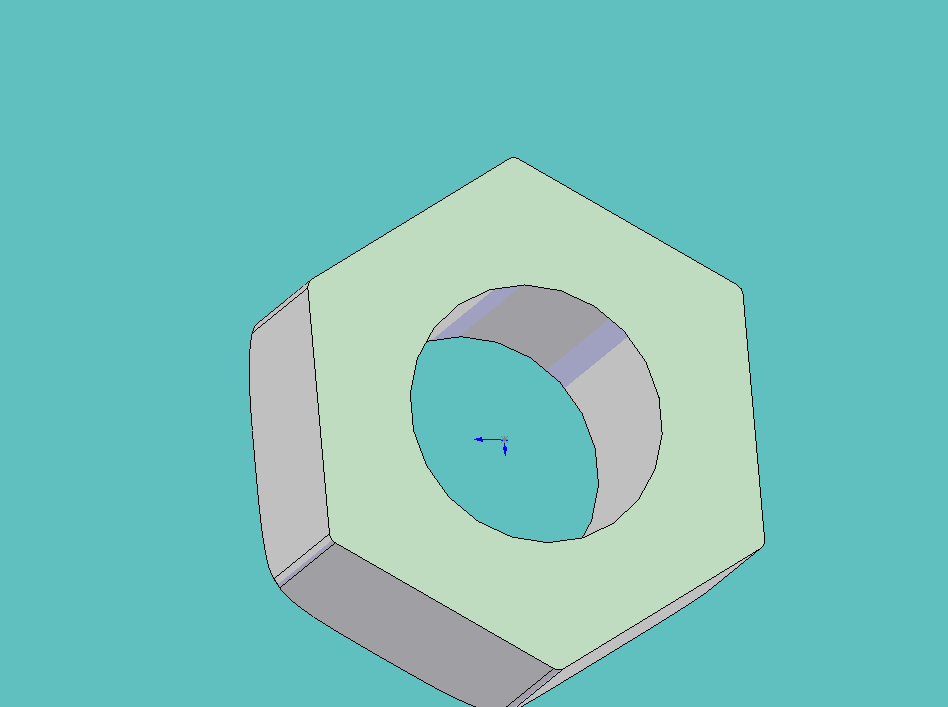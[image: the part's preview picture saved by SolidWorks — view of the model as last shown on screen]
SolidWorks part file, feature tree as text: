
SOLIDWORKS PART (.sldprt)
format: sldprt  version: not decoded by parser v0  size: 177,664 bytes
history: native  units: mm
features: sketch x2, material x1, extrude x1, cut_revolve x1, fillet x1, plane x1 (+13 scaffold rows collapsed)
feature tree (20):
  scaffold x13  (default folders/planes/origin — collapsed)
  material  "Material <not specified>"
  sketch  "Sketch1"  dims[D2=6.35mm D1=6.35mm]
  extrude  "Extrude1"  Depth=4.445mm
  sketch  "Sketch7"  dims[D1=0.508mm]
  cut_revolve  "Cut-Revolve2"  Angle=360deg
  fillet  "Fillet2"  Radius=0.254mm
  plane  "Plane1"  Offset=5.715mm
decode coverage: 5 of 5 modeling features carry decoded parameters
note: suppression state not decoded; provenance and decode notes live in map.json
